# Revit family: MUZ-AY20VG-E1,ET1
name_source: partatom
category: Mechanical Equipment
revit_build: Autodesk Revit 2018 (Build: 20181015_0930(x64)
units: mm (PartAtom-declared; Revit-internal decimal feet)

## family parameters
Always vertical = Yes
Cut with Voids When Loaded = No
OmniClass Number = 23.75.00.00
OmniClass Title = Climate Control (HVAC)
Part Type = Normal
Room Calculation Point = No
Round Connector Dimension = Use Diameter
Shared = No
Work Plane-Based = No

## types (1)
- MUZ-AY20VG-E1,ET1-230V50Hz
    Airflow  Cooling  High (m3/h) = 2178
    Airflow  Cooling  Low (m3/h) = 1038
    Airflow  Cooling  Medium (m3/h) = 2178
    Airflow  Heating  High (m3/h) = 2076
    Airflow  Heating  Low (m3/h) = 1284
    Airflow  Heating  Medium (m3/h) = 1788
    Breaker Capacity (A) = 10
    Capacity Rated (Min.-Max.)    Cooling (kW) = 2.0 (0.6 - 2.7)
    Capacity Rated (Min.-Max.)    Heating (kW) = 2.5 (0.5 - 3.5)
    Coefficient of performance (COP)(Set)  Cooling = 4.35
    Coefficient of performance (COP)(Set)  Heating = 4.17
    Compressor Current  Cooling (A) = 2.19
    Compressor Current  Heating (A) = 2.81
    Compressor Model = KVB073FYTMC
    Compressor Output (W) = 470
    Compressor Refrigeration oil (L) = 0.27
    Compressor Refrigeration oil (Model) = FW68S
    Dehumidification  Cooling (L/h) = 0.6
    Depth (mm) = 285 mm  [stored 0.935039 ft]
    Description = Outdoor unit
    Equip_No. = 0
    Fan motor  Current  Cooling (A) = 0.22
    Fan motor  Current  Heating (A) = 0.20
    Fan motor Model = RC0J50-NC
    Fan speed  Cooling  High (rpm) = 940
    Fan speed  Cooling  Low (rpm) = 470
    Fan speed  Cooling  Medium (rpm) = 940
    Fan speed  Heating  High (rpm) = 900
    Fan speed  Heating  Low (rpm) = 570
    Fan speed  Heating  Medium (rpm) = 780
    Fan speed regulator = 3
    Gas pipe O.D. (mm) = 9.52 mm
    Height (mm) = 550 mm
    Hertz = 50 Hz
    Liquid pipe O.D. (mm) = 6.35 mm  [stored 0.0208333 ft]
    Manufacturer = Mitsubishi Electric Corporation
    Model = MUZ-AY20VG
    Phase = 1
    Power factor (Set)  Cooling (%) = 76
    Power factor (Set)  Heating (%) = 81
    Power input (Set)  Cooiing (W) = 460
    Power input (Set)  Heating (W) = 600
    Refrigerant filling capacity (kg) = 0.55
    Refrigerant type = R32
    Running current (Set)  Cooling (A) = 2.6
    Running current (Set)  Heating (A) = 3.2
    SerialNumber = 0
    Sound level  Cooling (dB(A)) = 47
    Sound level  Heating (dB(A)) = 48
    Space View = Yes
    Starting current (Set) (A) = 3.2
    Subcategory = HVAC
    TagNumber = 0
    URL = https://www.mitsubishielectric.com
    Voltage = 230 V
    Weight (kg) = 27.5
    Width (mm) = 800 mm  [stored 2.62467 ft]

note: [stored X ft] marks values corroborated as IEEE doubles in the binary element streams (Revit-internal decimal feet)

## geometry (parser evidence)
native form markers: Blend x34, Sweep x2
no freeform markers — native parametric forms only
